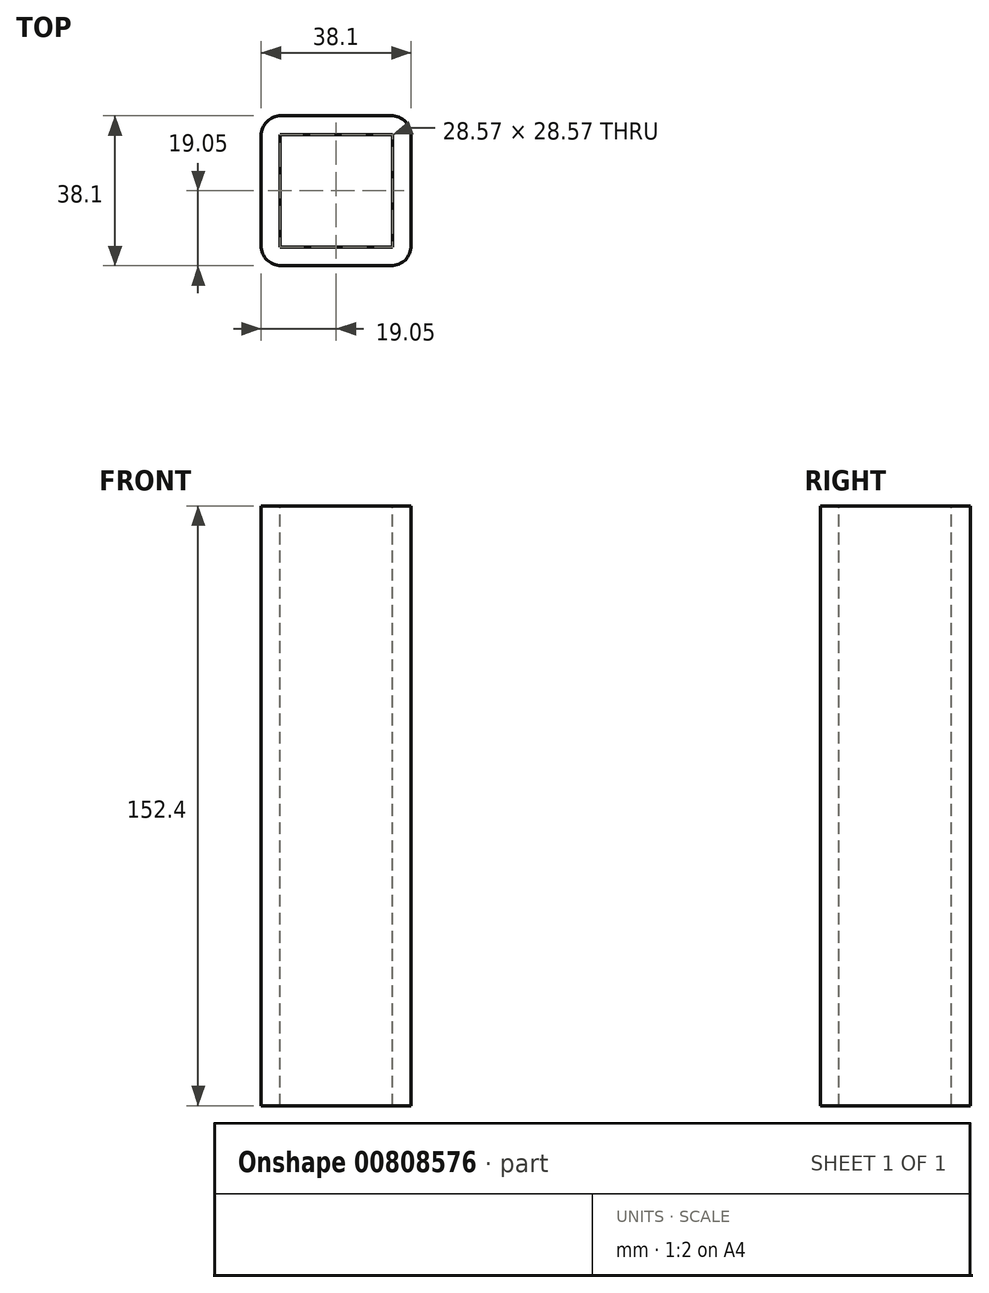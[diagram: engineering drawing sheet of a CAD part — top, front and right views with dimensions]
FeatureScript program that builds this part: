
annotation { "Feature Type Name" : "Feature", "Feature Type Description" : "" }
export const myFeature = defineFeature(function(context is Context, id is Id, definition is map)
    precondition{}
    {
        {
            var Q0;
            Q0=qCreatedBy(makeId("Top.planeOp"),FACE);
            var sketch = newSketch(context, id + "F0", { "sketchPlane" : qUnion([Q0])});
            skLineSegment(sketch, "E0.bottom", {"start": v(19.05, 19.05) * mm, "end": v(-19.05, 19.05) * mm});
            skLineSegment(sketch, "E0.top", {"start": v(19.05, -19.05) * mm, "end": v(-19.05, -19.05) * mm});
            skLineSegment(sketch, "E0.left", {"start": v(19.05, 19.05) * mm, "end": v(19.05, -19.05) * mm});
            skLineSegment(sketch, "E0.right", {"start": v(-19.05, 19.05) * mm, "end": v(-19.05, -19.05) * mm});
            skPoint(sketch, "E0.middle", {"position": v(0, 0) * mm});
            skLineSegment(sketch, "E1.0", {"start": v(14.29, 14.29) * mm, "end": v(-14.29, 14.29) * mm});
            skLineSegment(sketch, "E1.1", {"start": v(14.29, 14.29) * mm, "end": v(14.29, -14.29) * mm});
            skLineSegment(sketch, "E1.2", {"start": v(14.29, -14.29) * mm, "end": v(-14.29, -14.29) * mm});
            skLineSegment(sketch, "E1.3", {"start": v(-14.29, 14.29) * mm, "end": v(-14.29, -14.29) * mm});
            skSolve(sketch);
        }
        {
            var Q0;
            Q0=makeQuery(id+"F0.imprint","IMPRINT",FACE,{"disambiguationData":[TD([[makeQuery(id+"F0.imprint","IMPRINT",EDGE,{"derivedFrom":sQuery(id+"F0.wireOp",EDGE,"E0.bottom")}),1.0]])]});
            extrude(context, id + "F1", {"entities" : qUnion([Q0]), "oppositeDirection" : true, "depth" : 152.4 * mm, "offsetDistance" : 25.4 * mm});
        }
        {
            var Q0;
            Q0=makeQuery(id+"F1.opExtrude","SWEPT_EDGE",EDGE,{"disambiguationData":[OSD([sQuery(id+"F0.wireOp",EDGE,"E0.top"),sQuery(id+"F0.wireOp",EDGE,"E0.left")])]});
            var Q1;
            Q1=makeQuery(id+"F1.opExtrude","SWEPT_EDGE",EDGE,{"disambiguationData":[OSD([sQuery(id+"F0.wireOp",EDGE,"E0.bottom"),sQuery(id+"F0.wireOp",EDGE,"E0.left")])]});
            var Q2;
            Q2=makeQuery(id+"F1.opExtrude","SWEPT_EDGE",EDGE,{"disambiguationData":[OSD([sQuery(id+"F0.wireOp",EDGE,"E0.top"),sQuery(id+"F0.wireOp",EDGE,"E0.right")])]});
            var Q3;
            Q3=makeQuery(id+"F1.opExtrude","SWEPT_EDGE",EDGE,{"disambiguationData":[OSD([sQuery(id+"F0.wireOp",EDGE,"E0.bottom"),sQuery(id+"F0.wireOp",EDGE,"E0.right")])]});
            fillet(context, id + "F2", {"entities" : qUnion([Q0, Q1, Q2, Q3]), "radius" : 5.08 * mm, "tangentPropagation" : true, "allowEdgeOverflow" : false});
        }
    });
